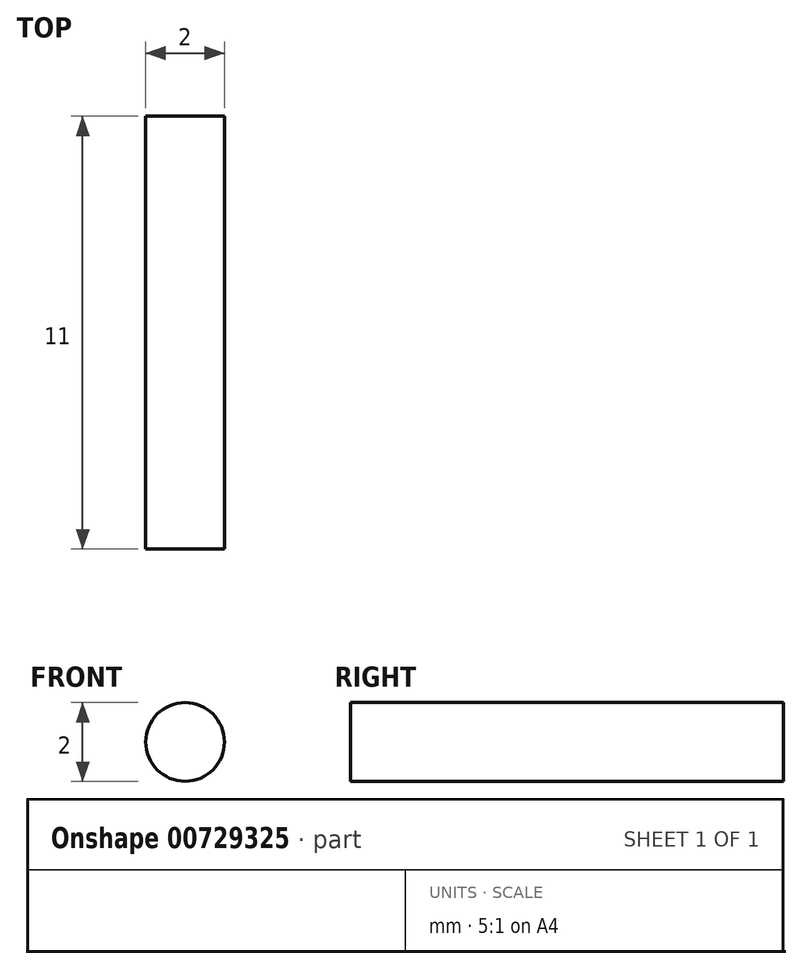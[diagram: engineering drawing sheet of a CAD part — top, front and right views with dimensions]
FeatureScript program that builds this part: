
annotation { "Feature Type Name" : "Feature", "Feature Type Description" : "" }
export const myFeature = defineFeature(function(context is Context, id is Id, definition is map)
    precondition{}
    {
        {
            var Q0;
            Q0=qCreatedBy(makeId("Front.planeOp"),FACE);
            var sketch = newSketch(context, id + "F0", { "sketchPlane" : qUnion([Q0])});
            skCircle(sketch, "E0", {"center": v(0, 0) * mm, "radius": 1 * mm});
            skSolve(sketch);
        }
        {
            var Q0;
            Q0=makeQuery(id+"F0.imprint","IMPRINT",FACE,{"disambiguationData":[TD([[makeQuery(id+"F0.imprint","IMPRINT",EDGE,{"derivedFrom":sQuery(id+"F0.wireOp",EDGE,"E0")}),1.0]])]});
            extrude(context, id + "F1", {"entities" : qUnion([Q0]), "depth" : 11 * mm, "offsetDistance" : 25 * mm});
        }
    });
